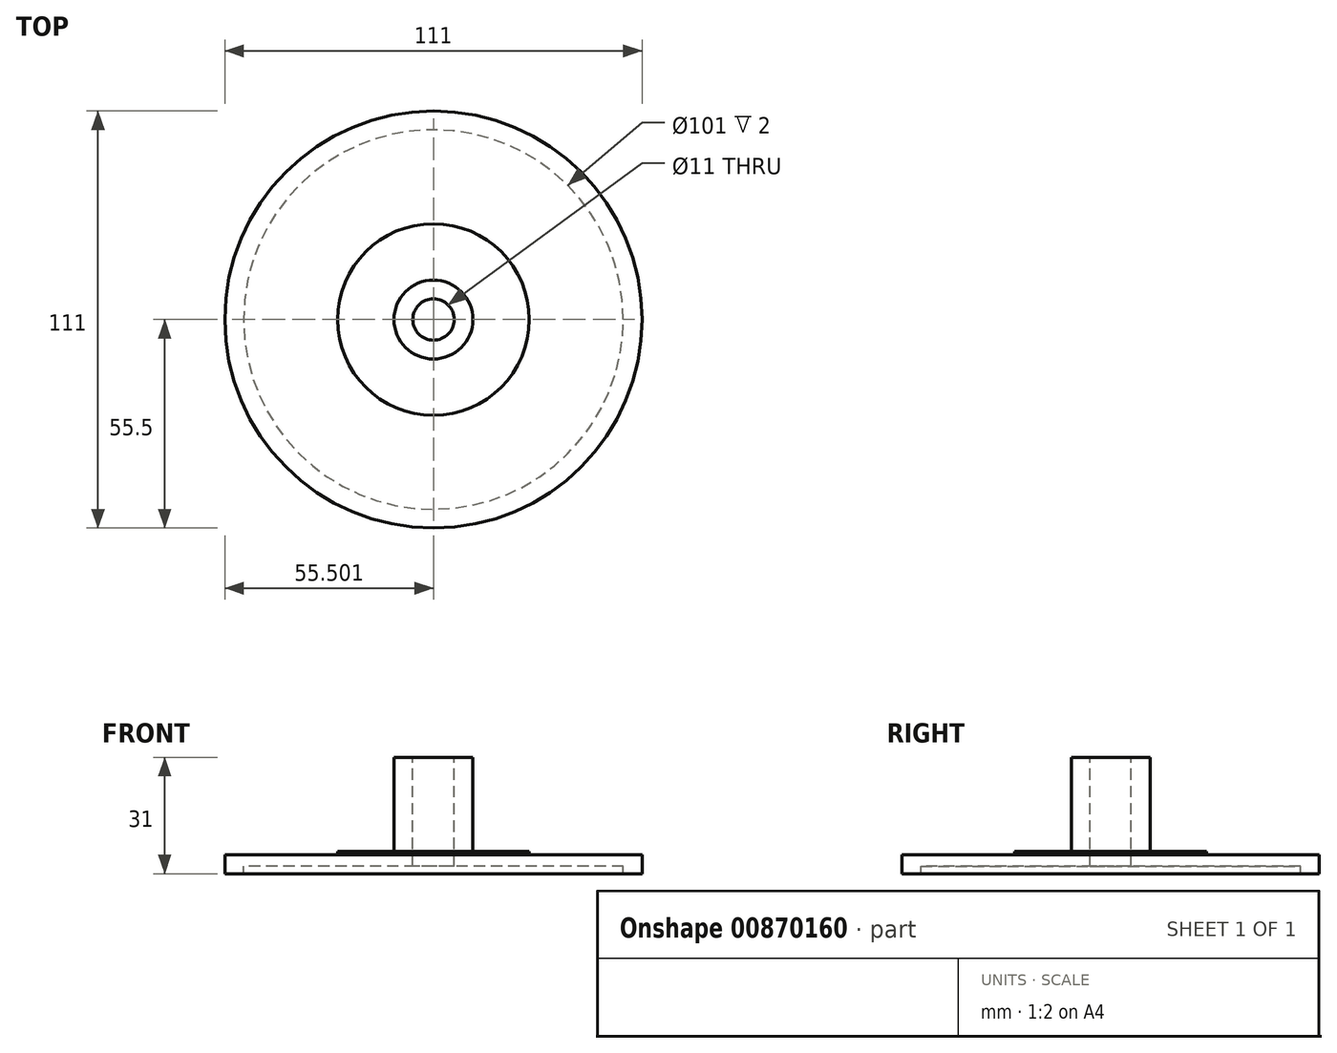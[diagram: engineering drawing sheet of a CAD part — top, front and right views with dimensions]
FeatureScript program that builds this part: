
annotation { "Feature Type Name" : "Feature", "Feature Type Description" : "" }
export const myFeature = defineFeature(function(context is Context, id is Id, definition is map)
    precondition{}
    {
        {
            var Q0;
            Q0=qCreatedBy(makeId("Front.planeOp"),FACE);
            var sketch = newSketch(context, id + "F0", { "sketchPlane" : qUnion([Q0])});
            skLineSegment(sketch, "E0", {"start": v(-47.27, 8.2) * mm, "end": v(-47.27, 13.2) * mm});
            skLineSegment(sketch, "E1", {"start": v(-17.27, 13.2) * mm, "end": v(-17.27, 14.2) * mm});
            skLineSegment(sketch, "E2", {"start": v(-17.27, 14.2) * mm, "end": v(-2.27, 14.2) * mm});
            skLineSegment(sketch, "E3", {"start": v(-2.27, 14.2) * mm, "end": v(-2.27, 39.2) * mm});
            skLineSegment(sketch, "E4", {"start": v(-2.27, 39.2) * mm, "end": v(2.73, 39.2) * mm});
            skLineSegment(sketch, "E5", {"start": v(2.73, 39.2) * mm, "end": v(2.73, 10.2) * mm});
            skLineSegment(sketch, "E6", {"start": v(2.73, 10.2) * mm, "end": v(-42.27, 10.2) * mm});
            skLineSegment(sketch, "E7", {"start": v(-42.27, 10.2) * mm, "end": v(-42.27, 8.2) * mm});
            skLineSegment(sketch, "E8", {"start": v(-42.27, 8.2) * mm, "end": v(-47.27, 8.2) * mm});
            skLineSegment(sketch, "E9", {"start": v(-47.27, 13.2) * mm, "end": v(-17.27, 13.2) * mm});
            skLineSegment(sketch, "E10", {"start": v(8.23, 46.1) * mm, "end": v(8.23, 3.46) * mm, "construction": true});
            skSolve(sketch);
        }
        {
            var Q0;
            Q0=makeQuery(id+"F0.imprint","IMPRINT",FACE,{"disambiguationData":[TD([[makeQuery(id+"F0.imprint","IMPRINT",EDGE,{"derivedFrom":sQuery(id+"F0.wireOp",EDGE,"E0")}),-1.0]])]});
            var Q1;
            Q1=sQuery(id+"F0.wireOp",EDGE,"E10");
            revolve(context, id + "F1", {"surfaceOperationType" : NewSurfaceOperationType.NEW, "entities" : qUnion([Q0]), "axis" : qUnion([Q1]), "revolveType" : RevolveType.FULL});
        }
    });
